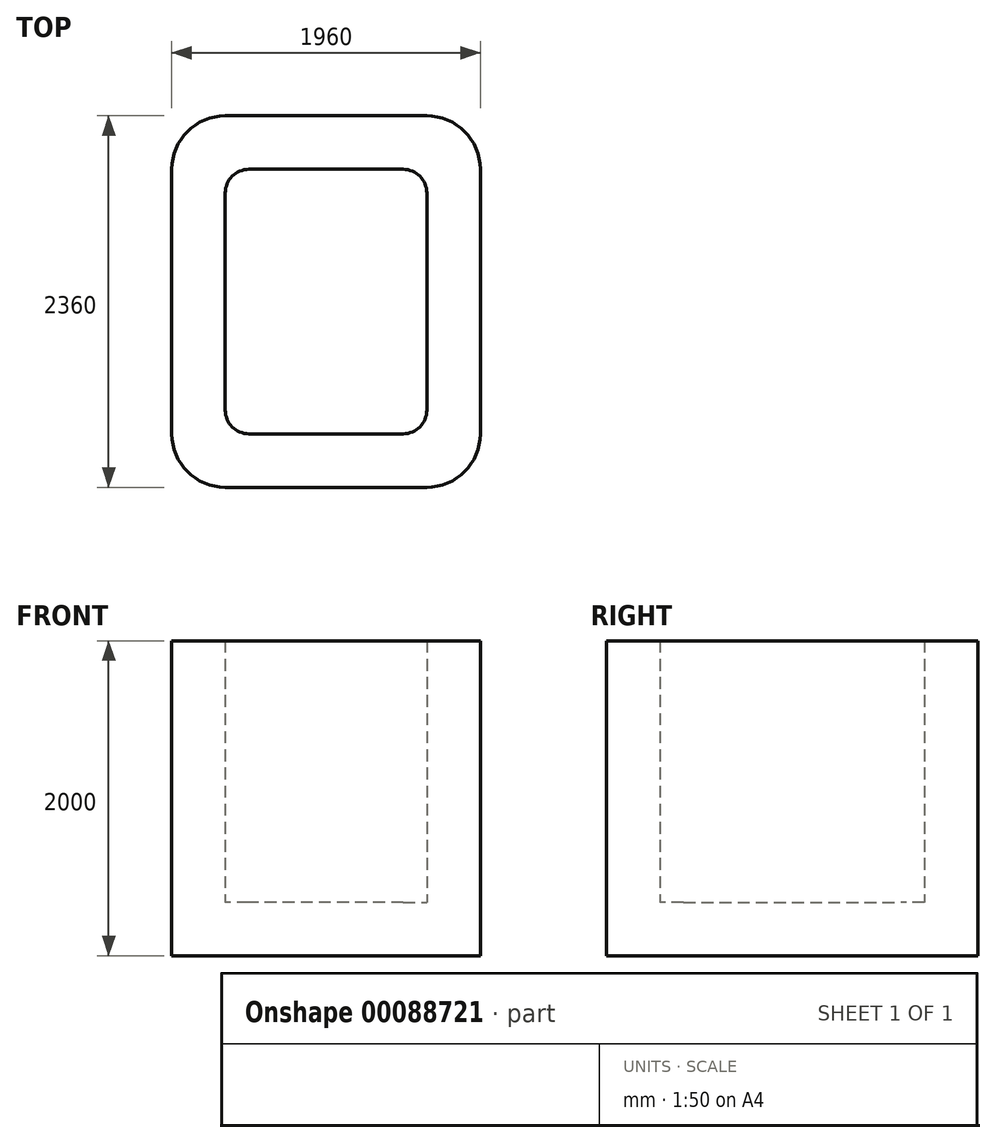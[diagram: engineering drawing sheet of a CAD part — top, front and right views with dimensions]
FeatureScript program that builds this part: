
annotation { "Feature Type Name" : "Feature", "Feature Type Description" : "" }
export const myFeature = defineFeature(function(context is Context, id is Id, definition is map)
    precondition{}
    {
        {
            var Q0;
            Q0=qCreatedBy(makeId("Top.planeOp"),FACE);
            var sketch = newSketch(context, id + "F0", { "sketchPlane" : qUnion([Q0])});
            skLineSegment(sketch, "E0.bottom", {"start": v(980, -1180) * mm, "end": v(-980, -1180) * mm});
            skLineSegment(sketch, "E0.top", {"start": v(980, 1180) * mm, "end": v(-980, 1180) * mm});
            skLineSegment(sketch, "E0.left", {"start": v(980, -1180) * mm, "end": v(980, 1180) * mm});
            skLineSegment(sketch, "E0.right", {"start": v(-980, -1180) * mm, "end": v(-980, 1180) * mm});
            skPoint(sketch, "E0.middle", {"position": v(0, 0) * mm});
            skSolve(sketch);
        }
        {
            var Q0;
            Q0 = qSketchRegion(id + "F0", true);
            var Q1;
            Q1=makeQuery(id+"F0.imprint","IMPRINT",FACE,{"disambiguationData":[TD([[makeQuery(id+"F0.imprint","IMPRINT",EDGE,{"derivedFrom":sQuery(id+"F0.wireOp",EDGE,"E0.bottom")}),-1.0]])]});
            extrude(context, id + "F1", {"entities" : qUnion([Q0, Q1]), "depth" : 2000 * mm});
        }
        {
            var Q0;
            Q0=makeQuery(id+"F1.opExtrude","CAP_FACE",FACE,{"disambiguationData":[OSD([sQuery(id+"F0.wireOp",EDGE,"E0.bottom"),sQuery(id+"F0.wireOp",EDGE,"E0.top"),sQuery(id+"F0.wireOp",EDGE,"E0.left"),sQuery(id+"F0.wireOp",EDGE,"E0.right")])],"isStart":false});
            shell(context, id + "F2", {"entities" : qUnion([Q0]), "thickness" : 340 * mm});
        }
        {
            var Q0;
            Q0=makeQuery(id+"F1.opExtrude","SWEPT_EDGE",EDGE,{"disambiguationData":[OSD([sQuery(id+"F0.wireOp",EDGE,"E0.top"),sQuery(id+"F0.wireOp",EDGE,"E0.right")])]});
            var Q1;
            Q1=makeQuery(id+"F1.opExtrude","SWEPT_EDGE",EDGE,{"disambiguationData":[OSD([sQuery(id+"F0.wireOp",EDGE,"E0.top"),sQuery(id+"F0.wireOp",EDGE,"E0.left")])]});
            var Q2;
            Q2=makeQuery(id+"F1.opExtrude","SWEPT_EDGE",EDGE,{"disambiguationData":[OSD([sQuery(id+"F0.wireOp",EDGE,"E0.bottom"),sQuery(id+"F0.wireOp",EDGE,"E0.right")])]});
            var Q3;
            Q3=makeQuery(id+"F1.opExtrude","SWEPT_EDGE",EDGE,{"disambiguationData":[OSD([sQuery(id+"F0.wireOp",EDGE,"E0.bottom"),sQuery(id+"F0.wireOp",EDGE,"E0.left")])]});
            fillet(context, id + "F3", {"entities" : qUnion([Q0, Q1, Q2, Q3]), "radius" : 340 * mm, "tangentPropagation" : true, "allowEdgeOverflow" : false});
        }
        {
            var Q0;
            Q0=makeQuery(id+"F2.opShell","OFFSET_EDGE",EDGE,{"disambiguationData":[OSD([sQuery(id+"F0.wireOp",EDGE,"E0.top"),sQuery(id+"F0.wireOp",EDGE,"E0.left")])]});
            var Q1;
            Q1=makeQuery(id+"F2.opShell","OFFSET_EDGE",EDGE,{"disambiguationData":[OSD([sQuery(id+"F0.wireOp",EDGE,"E0.bottom"),sQuery(id+"F0.wireOp",EDGE,"E0.left")])]});
            var Q2;
            Q2=makeQuery(id+"F2.opShell","OFFSET_EDGE",EDGE,{"disambiguationData":[OSD([sQuery(id+"F0.wireOp",EDGE,"E0.bottom"),sQuery(id+"F0.wireOp",EDGE,"E0.right")])]});
            var Q3;
            Q3=makeQuery(id+"F2.opShell","OFFSET_EDGE",EDGE,{"disambiguationData":[OSD([sQuery(id+"F0.wireOp",EDGE,"E0.top"),sQuery(id+"F0.wireOp",EDGE,"E0.right")])]});
            fillet(context, id + "F4", {"entities" : qUnion([Q0, Q1, Q2, Q3]), "radius" : 150 * mm, "tangentPropagation" : true, "allowEdgeOverflow" : false});
        }
    });
